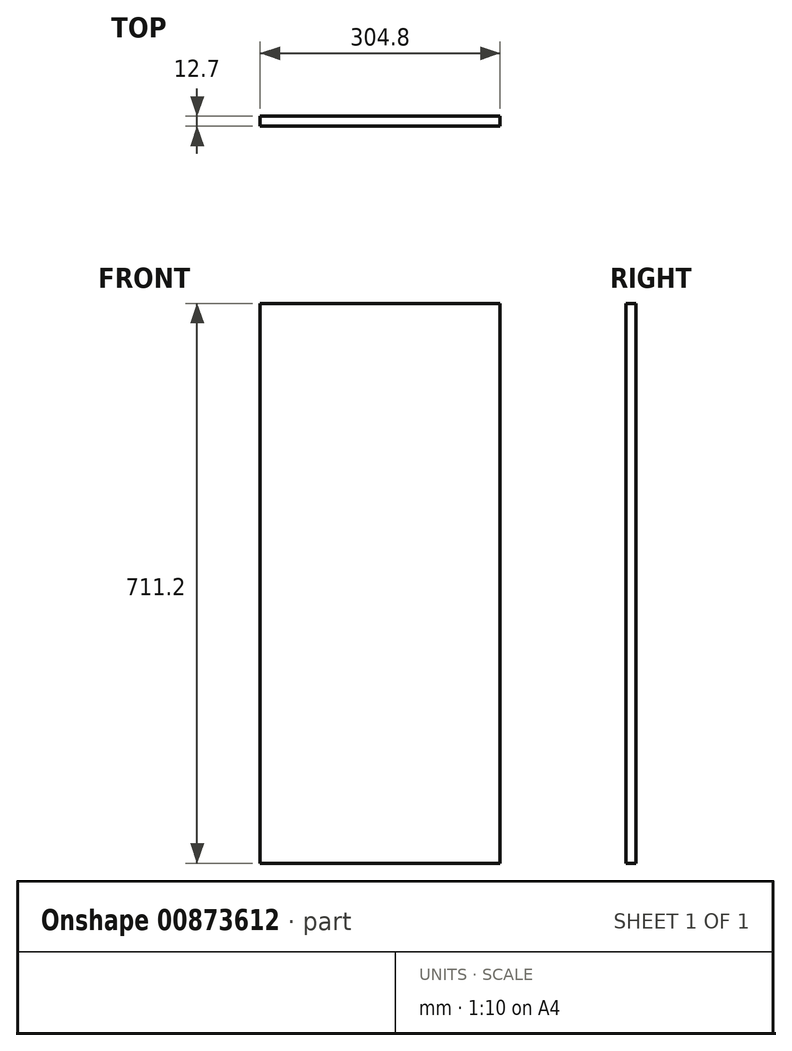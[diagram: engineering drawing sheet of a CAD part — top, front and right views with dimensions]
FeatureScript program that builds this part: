
annotation { "Feature Type Name" : "Feature", "Feature Type Description" : "" }
export const myFeature = defineFeature(function(context is Context, id is Id, definition is map)
    precondition{}
    {
        {
            var Q0;
            Q0=qCreatedBy(makeId("Front.planeOp"),FACE);
            var sketch = newSketch(context, id + "F0", { "sketchPlane" : qUnion([Q0])});
            skLineSegment(sketch, "E0.bottom", {"start": v(0, 0) * mm, "end": v(304.8, 0) * mm});
            skLineSegment(sketch, "E0.top", {"start": v(0, 711.2) * mm, "end": v(304.8, 711.2) * mm});
            skLineSegment(sketch, "E0.left", {"start": v(0, 0) * mm, "end": v(0, 711.2) * mm});
            skLineSegment(sketch, "E0.right", {"start": v(304.8, 0) * mm, "end": v(304.8, 711.2) * mm});
            skSolve(sketch);
        }
        {
            var Q0;
            Q0 = qSketchRegion(id + "F0", true);
            extrude(context, id + "F1", {"entities" : qUnion([Q0]), "depth" : 12.7 * mm, "offsetDistance" : 25.4 * mm});
        }
    });
